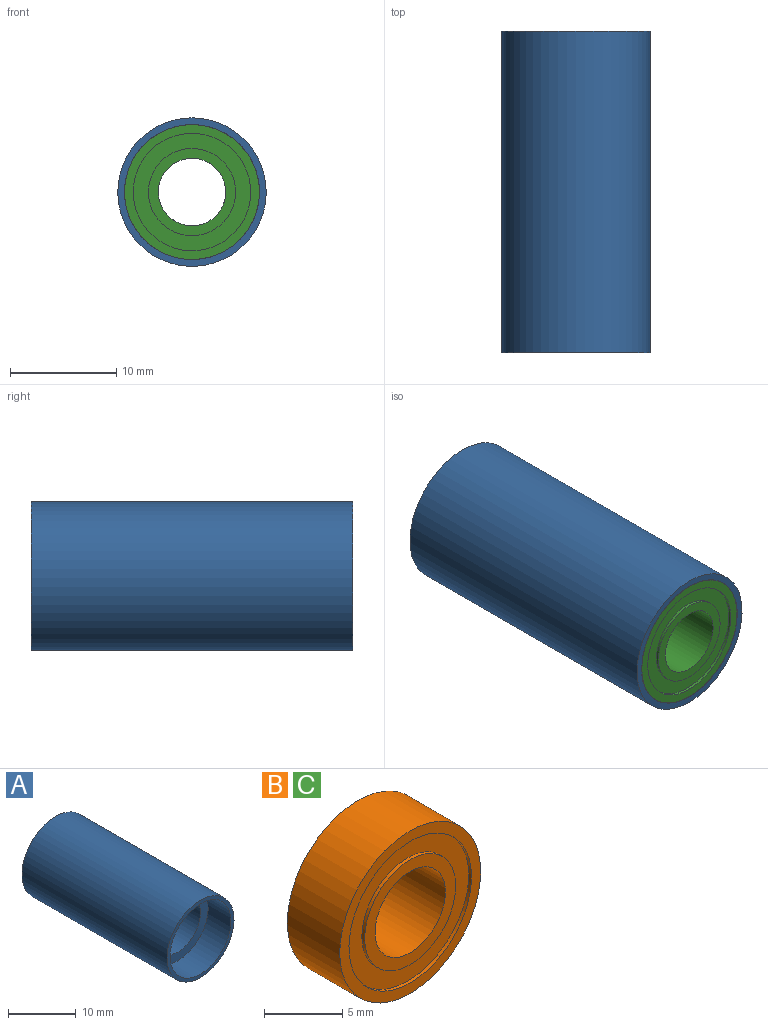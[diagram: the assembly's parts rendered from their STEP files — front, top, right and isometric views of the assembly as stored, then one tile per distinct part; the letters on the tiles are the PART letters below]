
ASSEMBLY  parts=3 mates=1
PART A: 8 faces, bbox 14x30.2x14 mm
  f0: cylinder r=6.35mm len=12.7mm, axis (0,-1,0), area 190mm2, adj f4,f7
  f1: cylinder r=6.35mm len=12.7mm, axis (0,1,0), area 190mm2, adj f5,f6
  f2: cylinder r=6.99mm len=30.23mm, axis (0,-1,0), area 1326.6mm2, adj f4,f5
  f3: cylinder r=4.76mm len=20.7mm, axis (0,-1,0), area 619.4mm2, adj f6,f7
  f4: plane 13.97x13.97mm, normal (0,-1,0), area 26.6mm2, adj f0,f2
  f5: plane 13.97x13.97mm, normal (0,1,0), area 26.6mm2, adj f1,f2
  f6: plane 12.7x12.7mm, normal (0,1,0), area 55.4mm2, adj f1,f3
  f7: plane 12.7x12.7mm, normal (0,-1,0), area 55.4mm2, adj f0,f3
PART B: 12 faces, bbox 12.7x4.7x12.7 mm
  f0: cylinder r=4.1mm len=8.2mm, axis (0,-1,0), area 6.5mm2, adj f6,f11
  f1: cylinder r=5.52mm len=11.05mm, axis (0,-1,0), area 8.8mm2, adj f9,f11
  f2: cylinder r=4.1mm len=8.2mm, axis (0,1,0), area 6.5mm2, adj f7,f10
  f3: cylinder r=5.52mm len=11.05mm, axis (0,1,0), area 8.8mm2, adj f8,f10
  f4: cylinder r=3.17mm len=6.35mm, axis (0,-1,0), area 94.2mm2, adj f6,f7
  f5: cylinder r=6.35mm len=12.7mm, axis (0,-1,0), area 188.5mm2, adj f8,f9
  f6: plane 8.2x8.2mm, normal (0,-1,0), area 21.2mm2, adj f0,f4
  f7: plane 8.2x8.2mm, normal (0,1,0), area 21.2mm2, adj f2,f4
  f8: plane 12.7x12.7mm, normal (0,1,0), area 30.8mm2, adj f3,f5
  f9: plane 12.7x12.7mm, normal (0,-1,0), area 30.8mm2, adj f1,f5
  f10: plane 11.05x11.05mm, normal (0,1,0), area 43mm2, adj f2,f3
  f11: plane 11.05x11.05mm, normal (0,-1,0), area 43mm2, adj f0,f1
PART C: same geometry as B
PLACE A t=(-44.78,-17.27,25.1)mm
PLACE B t=(-44.78,8.19,25.1)mm
PLACE C rot(axis=(0,1,0),16.3deg) t=(-44.78,-17.24,25.1)mm
MATE fastened B.f0 <-> A.f0  axis (0,1,0) through (-44.78,12.91,25.1)mm
